# Revit family: Indoor_Table Lamp_Santa&Cole_Básica M1-M2
name_source: partatom
category: Luminarias
revit_build: Autodesk Revit 2018 (Build: 20190510_1515(x64)
units: mm (PartAtom-declared; Revit-internal decimal feet)

## family parameters
Compartido = No
Corte con vacíos al cargar = No
Cota de conector redondo = Diámetro de uso
Número OmniClass = 23.80.70.00
Origen de luz = Sí
Punto de cálculo de habitación = No
Se basa en plano de trabajo = No
Siempre vertical = Sí
Tipo de pieza = Normal
Título OmniClass = Lighting

## types (18) — shared parameters
Assembly instructions - CE = https://www.santacole.com
Assembly instructions - UL = https://www.santacole.com
Cambio de temperatura de color de luz atenuada = <Ninguno>
Carga aparente = 10 VA
Energy Label = https://www.santacole.com
Fabricante = Santa & Cole
Filtro de color = 16777215
Load = 10 W
Manufacturer website = http://www.santacole.com
Modelo = Básica
Tamaño de símbolo de origen de luz = 50 mm  [stored 0.164042 ft]
Technical Information = https://www.santacole.com
URL = https://www.santacole.com

## per-type parameters (varying)
| type | Code | Height_Stabilizing Base | Lampshade Material | Visibility_Lamp M1 | Visibility_Lamp M2 | Visibility_M1_Beige Parchment | Visibility_M2_Beige Parchment | Visibility_Stabilizing Base |
| M2 - Stitched Beige Parchment Lampshade | BASAx+PM10x | 0 mm  [stored 0 ft] | Santa & Cole - Beige Cardboard | No | Sí | No | Sí | No |
| M2 - Stitched Beige Parchment Lampshade with Stabilizing Base | BASAx+PM10x+6BAS0x | 2 mm  [stored 0.00656168 ft] | Santa & Cole - Beige Cardboard | No | Sí | No | Sí | Sí |
| M1 - Stitched Beige Parchment Lampshade | BASAx+PM10x | 0 mm  [stored 0 ft] | Santa & Cole - Beige Cardboard | Sí | No | Sí | No | No |
| M1 - Natural Ribbon Lampshade | BASAx+PM10x | 0 mm  [stored 0 ft] | Santa & Cole - Natural Ribbon | Sí | No | No | No | No |
| M1 - Red-amber Ribbon Lampshade | BASAx+PM10x | 0 mm  [stored 0 ft] | Santa & Cole - Red-amber Ribbon | Sí | No | No | No | No |
| M1 - Black Ribbon Lampshade | BASAx+PM10x | 0 mm  [stored 0 ft] | Santa & Cole - Black Ribbon | Sí | No | No | No | No |
| M1 - Terracota Raw Color Ribbon Lampshade | BASAx+PM10x | 0 mm  [stored 0 ft] | Santa & Cole - Terracota Raw Color Ribbon | Sí | No | No | No | No |
| M1 - Mustard Raw Color Ribbon Lampshade | BASAx+PM10x | 0 mm  [stored 0 ft] | Santa & Cole - Mustard Raw Color Ribbon | Sí | No | No | No | No |
| M1 - Green Raw Color Ribbon Lampshade | BASAx+PM10x | 0 mm  [stored 0 ft] | Santa & Cole - Green Raw Color Ribbon | Sí | No | No | No | No |
| M1 - White Linen Lampshade | BASAx+PM10x | 0 mm  [stored 0 ft] | Santa & Cole - White Linen | Sí | No | No | No | No |
| M1 - Black Ribbon Lampshade with Stabilizing Base | BASAx+PM10x+6BAS0x | 2 mm  [stored 0.00656168 ft] | Santa & Cole - Black Ribbon | Sí | No | No | No | Sí |
| M1 - Natural Ribbon Lampshade with Stabilizing Base | BASAx+PM10x+6BAS0x | 2 mm  [stored 0.00656168 ft] | Santa & Cole - Natural Ribbon | Sí | No | No | No | Sí |
| M1 - Stitched Beige Parchment Lampshade with Stabilizing Base | BASAx+PM10x+6BAS0x | 2 mm  [stored 0.00656168 ft] | Santa & Cole - Beige Cardboard | Sí | No | No | No | Sí |
| M1 - Red-amber Ribbon Lampshade with Stabilizing Base | BASAx+PM10x+6BAS0x | 2 mm  [stored 0.00656168 ft] | Santa & Cole - Red-amber Ribbon | Sí | No | No | No | Sí |
| M1 - Terracota Raw Color Ribbon Lampshade with Stabilizing Base | BASAx+PM10x+6BAS0x | 2 mm  [stored 0.00656168 ft] | Santa & Cole - Terracota Raw Color Ribbon | Sí | No | No | No | Sí |
| M1 - Mustard Raw Color Ribbon Lampshade with Stabilizing Base | BASAx+PM10x+6BAS0x | 2 mm  [stored 0.00656168 ft] | Santa & Cole - Mustard Raw Color Ribbon | Sí | No | No | No | Sí |
| M1 - Green Raw Color Ribbon Lampshade with Stabilizing Base | BASAx+PM10x+6BAS0x | 2 mm  [stored 0.00656168 ft] | Santa & Cole - Green Raw Color Ribbon | Sí | No | No | No | Sí |
| M1 - White Linen Lampshade with Stabilizing Base | BASAx+PM10x+6BAS0x | 2 mm  [stored 0.00656168 ft] | Santa & Cole - White Linen | Sí | No | No | No | Sí |

note: [stored X ft] marks values corroborated as IEEE doubles in the binary element streams (Revit-internal decimal feet)

## geometry (parser evidence)
native form markers: Sweep x2
no freeform markers — native parametric forms only
